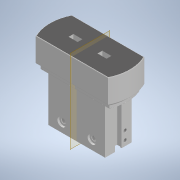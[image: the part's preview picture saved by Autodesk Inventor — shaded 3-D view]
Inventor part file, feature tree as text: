
AUTODESK INVENTOR PART (.ipt)
format: ipt  version: 2021 (Build 250183000, 183)  size: 371,200 bytes
history: native  units: mm
features: other x28, sketch x16, revolve x8, extrude x6, thread x5, hole x2, plane x2
ambient origin geometry x8: Origin, YZ Plane, XZ Plane, XY Plane, X Axis, Y Axis, Z Axis, Center Point
bodies: Solid1 (feature_tree)
feature tree (67):
  extrude  "Extrusion1"  TaperAngle=360.0deg  [1 undecoded]
  hole  "Hole1"  [1 undecoded]
  hole  "Hole2"  [1 undecoded]
  revolve  "Revolution1"  Angle=360.0deg
  thread  "Thread1"  [1 undecoded]
  extrude  "Extrusion2"  TaperAngle=360.0deg  [1 undecoded]
  extrude  "Extrusion3"  TaperAngle=360.0deg  [1 undecoded]
  revolve  "Revolution2"  [1 undecoded]
  thread  "Thread2"  [1 undecoded]
  revolve  "Revolution3"  [1 undecoded]
  revolve  "Revolution4"  [1 undecoded]
  thread  "Thread3"  [1 undecoded]
  revolve  "Revolution5"  [1 undecoded]
  thread  "Thread4"  [1 undecoded]
  revolve  "Revolution6"  [1 undecoded]
  thread  "Thread5"  [1 undecoded]
  extrude  "Extrusion4"  [1 undecoded]
  revolve  "Revolution7"  [1 undecoded]
  revolve  "Revolution8"  [1 undecoded]
  extrude  "Extrusion5"  [1 undecoded]
  extrude  "Extrusion6"  [1 undecoded]
  other  "JAW_1_XY"
  other  "JAW_1_YZ"
  other  "JAW_1_ZX"
  other  "JAW_1_X"
  other  "JAW_1_Y"
  other  "JAW_1_Z"
  other  "JAW_1_Center"
  other  "JAW_2_XY"
  other  "JAW_2_YZ"
  other  "JAW_2_ZX"
  other  "JAW_2_X"
  other  "JAW_2_Y"
  other  "JAW_2_Z"
  other  "JAW_2_Center"
  other  "ZBH_1_XY"
  other  "ZBH_1_YZ"
  other  "ZBH_1_ZX"
  other  "ZBH_1_X"
  other  "ZBH_1_Y"
  other  "ZBH_1_Z"
  other  "ZBH_1_Center"
  other  "ZBH_2_XY"
  other  "ZBH_2_YZ"
  other  "ZBH_2_ZX"
  other  "ZBH_2_X"
  other  "ZBH_2_Y"
  other  "ZBH_2_Z"
  other  "ZBH_2_Center"
  plane  "Work Plane13"
  plane  "Work Plane14"
  sketch  "Sketch_1"  dims[d0=22.0mm d1=0.0mm]
  sketch  "Sketch2"  dims[d2=2.459mm d3=3.5mm d4=3.0mm d5=2.0mm d6=90.0deg d7=3.5mm d8=0.0mm]
  sketch  "Sketch3"  dims[d9=2.459mm d10=3.5mm d11=3.0mm d12=2.0mm d13=90.0deg d14=3.5mm d15=0.0mm d16=360.0deg]
  sketch  "Sketch_7"  dims[d39=90.0deg d40=7.5mm d41=0.0mm]
  sketch  "Sketch_8"  dims[d42=7.5mm d43=0.0mm d44=0.0mm d45=0.0mm]
  sketch  "Sketch_9"  dims[d46=0.0mm d47=0.0mm]
  sketch  "Sketch_4"  dims[d21=81.2mm d22=0.0mm d23=360.0deg]
  sketch  "Sketch_14"
  sketch  "Sketch_5"  dims[d28=5.521mm d29=0.0mm d30=360.0deg]
  sketch  "Sketch_15"
  sketch  "Sketch_6"  dims[d34=6.621mm d35=0.0mm d36=67.0mm d37=0.0mm d38=90.0deg]
  sketch  "Skizze_3"  dims[d17=6.621mm d18=0.0mm d19=81.2mm d20=0.0mm]
  sketch  "Skizze_4"  dims[d24=5.521mm d25=0.0mm d26=360.0deg d27=360.0deg]
  sketch  "Skizze_5"  dims[d31=5.521mm d32=0.0mm d33=360.0deg]
  sketch  "Sketch_10"
  sketch  "Sketch_11"
note: 20 required parameter values undecoded (feature->parameter linkage not recoverable at this tier; creation-order binding heuristic only, values carry confidence <= 0.55)